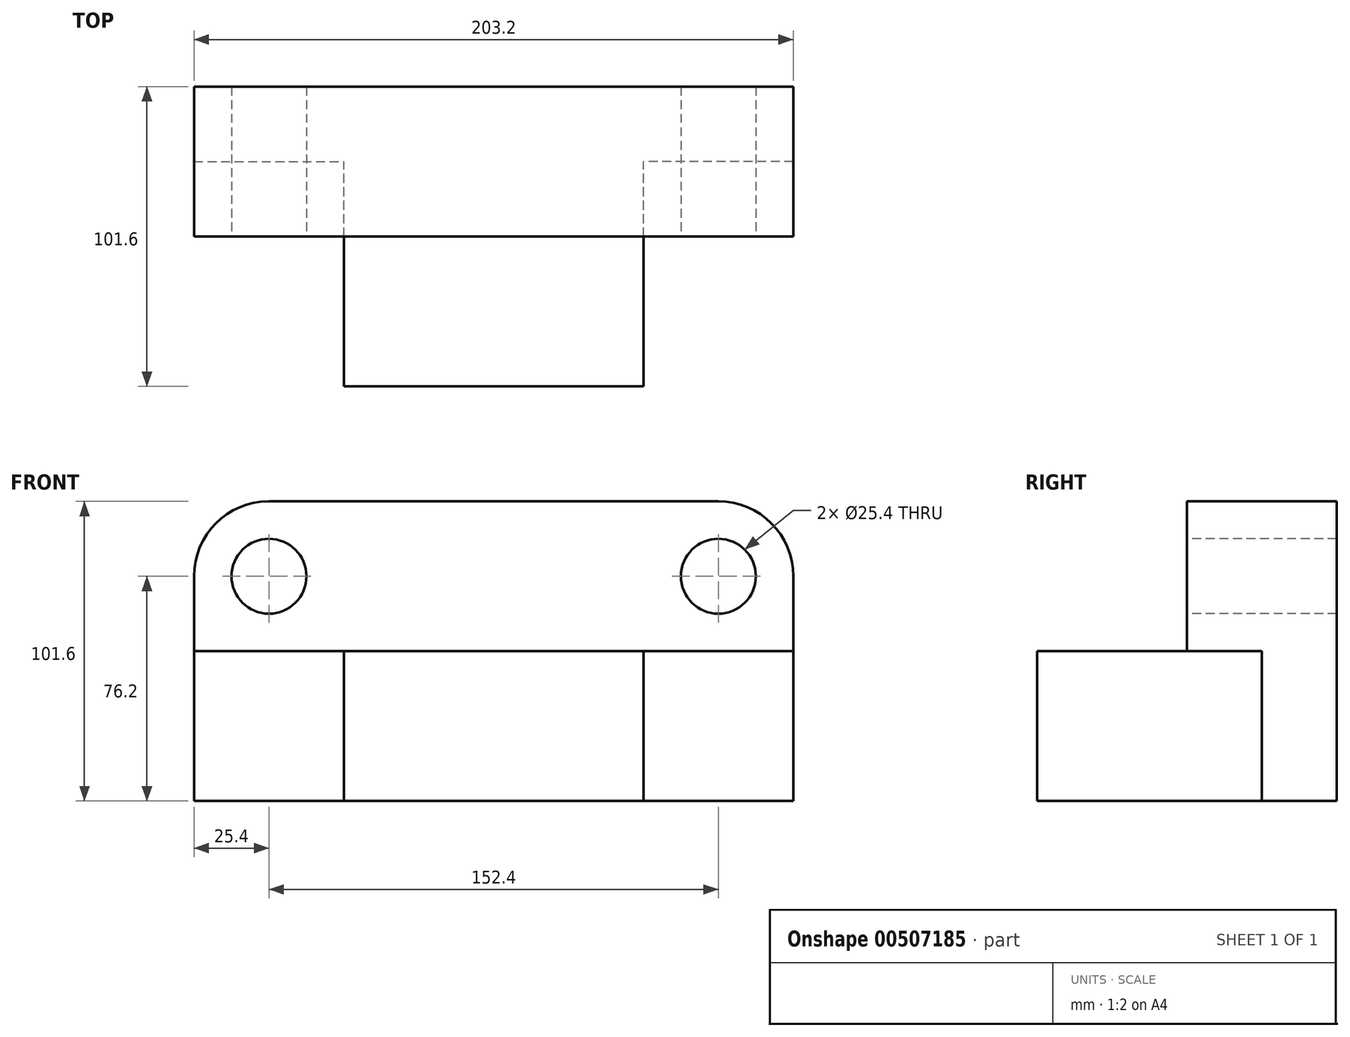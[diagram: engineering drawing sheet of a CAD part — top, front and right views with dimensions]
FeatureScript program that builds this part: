
annotation { "Feature Type Name" : "Feature", "Feature Type Description" : "" }
export const myFeature = defineFeature(function(context is Context, id is Id, definition is map)
    precondition{}
    {
        {
            var Q0;
            Q0=qCreatedBy(makeId("Top.planeOp"),FACE);
            var sketch = newSketch(context, id + "F0", { "sketchPlane" : qUnion([Q0])});
            skLineSegment(sketch, "E0.bottom", {"start": v(0, 0) * mm, "end": v(203.2, 0) * mm});
            skLineSegment(sketch, "E0.top", {"start": v(0, -101.6) * mm, "end": v(203.2, -101.6) * mm});
            skLineSegment(sketch, "E0.left", {"start": v(0, 0) * mm, "end": v(0, -101.6) * mm});
            skLineSegment(sketch, "E0.right", {"start": v(203.2, 0) * mm, "end": v(203.2, -101.6) * mm});
            skSolve(sketch);
        }
        {
            var Q0;
            Q0=makeQuery(id+"F0.imprint","IMPRINT",FACE,{"disambiguationData":[TD([[makeQuery(id+"F0.imprint","IMPRINT",EDGE,{"derivedFrom":sQuery(id+"F0.wireOp",EDGE,"E0.bottom")}),-1.0]])]});
            extrude(context, id + "F1", {"entities" : qUnion([Q0]), "depth" : 101.6 * mm});
        }
        {
            var Q0;
            Q0=makeQuery(id+"F1.opExtrude","CAP_FACE",FACE,{"disambiguationData":[OSD([sQuery(id+"F0.wireOp",EDGE,"E0.bottom"),sQuery(id+"F0.wireOp",EDGE,"E0.top"),sQuery(id+"F0.wireOp",EDGE,"E0.left"),sQuery(id+"F0.wireOp",EDGE,"E0.right")])],"isStart":true});
            var sketch = newSketch(context, id + "F2", { "sketchPlane" : qUnion([Q0])});
            skLineSegment(sketch, "E1.bottom", {"start": v(203.2, 101.6) * mm, "end": v(152.4, 101.6) * mm});
            skLineSegment(sketch, "E1.top", {"start": v(203.2, 25.4) * mm, "end": v(152.4, 25.4) * mm});
            skLineSegment(sketch, "E1.left", {"start": v(203.2, 101.6) * mm, "end": v(203.2, 25.4) * mm});
            skLineSegment(sketch, "E1.right", {"start": v(152.4, 101.6) * mm, "end": v(152.4, 25.4) * mm});
            skSolve(sketch);
        }
        {
            var Q0;
            Q0=makeQuery(id+"F2.imprint","IMPRINT",FACE,{"disambiguationData":[TD([[makeQuery(id+"F2.imprint","IMPRINT",EDGE,{"derivedFrom":sQuery(id+"F2.wireOp",EDGE,"E1.bottom")}),-1.0]])]});
            extrude(context, id + "F3", {"entities" : qUnion([Q0]), "operationType" : NewBodyOperationType.REMOVE, "oppositeDirection" : true, "depth" : 50.8 * mm});
        }
        {
            var Q0;
            Q0=makeQuery(id+"F1.opExtrude","CAP_FACE",FACE,{"disambiguationData":[OSD([sQuery(id+"F0.wireOp",EDGE,"E0.bottom"),sQuery(id+"F0.wireOp",EDGE,"E0.top"),sQuery(id+"F0.wireOp",EDGE,"E0.left"),sQuery(id+"F0.wireOp",EDGE,"E0.right")])],"isStart":true});
            var sketch = newSketch(context, id + "F4", { "sketchPlane" : qUnion([Q0])});
            skLineSegment(sketch, "E2.bottom", {"start": v(0, 101.6) * mm, "end": v(50.8, 101.6) * mm});
            skLineSegment(sketch, "E2.top", {"start": v(0, 25.4) * mm, "end": v(50.8, 25.4) * mm});
            skLineSegment(sketch, "E2.left", {"start": v(0, 101.6) * mm, "end": v(0, 25.4) * mm});
            skLineSegment(sketch, "E2.right", {"start": v(50.8, 101.6) * mm, "end": v(50.8, 25.4) * mm});
            skSolve(sketch);
        }
        {
            var Q0;
            Q0=makeQuery(id+"F4.imprint","IMPRINT",FACE,{"disambiguationData":[TD([[makeQuery(id+"F4.imprint","IMPRINT",EDGE,{"derivedFrom":sQuery(id+"F4.wireOp",EDGE,"E2.bottom")}),-1.0]])]});
            extrude(context, id + "F5", {"entities" : qUnion([Q0]), "operationType" : NewBodyOperationType.REMOVE, "oppositeDirection" : true, "depth" : 50.8 * mm});
        }
        {
            var Q0;
            Q0=makeQuery(id+"F1.opExtrude","CAP_EDGE",EDGE,{"disambiguationData":[OSD([sQuery(id+"F0.wireOp",EDGE,"E0.right")])],"isStart":false});
            fillet(context, id + "F6", {"entities" : qUnion([Q0]), "radius" : 25.4 * mm, "tangentPropagation" : true, "allowEdgeOverflow" : false});
        }
        {
            var Q0;
            Q0=makeQuery(id+"F1.opExtrude","CAP_EDGE",EDGE,{"disambiguationData":[OSD([sQuery(id+"F0.wireOp",EDGE,"E0.left")])],"isStart":false});
            fillet(context, id + "F7", {"entities" : qUnion([Q0]), "radius" : 25.4 * mm, "tangentPropagation" : true, "allowEdgeOverflow" : false});
        }
        {
            var Q0;
            Q0=makeQuery(id+"F4PwHQEw8X9MmWq_1.boolean.opBoolean","COPY",FACE,{"derivedFrom":makeQuery(id+"F4PwHQEw8X9MmWq_1.opExtrude","SWEPT_FACE",FACE,{"disambiguationData":[OSD([sQuery(id+"FQOh0idirYJ9PJE_1.wireOp",EDGE,"Frty84uf-Vyrj-mid0-v118-2i0YeY8wPQO7.top")])]})});
            var sketch = newSketch(context, id + "F8", { "sketchPlane" : qUnion([Q0])});
            skCircle(sketch, "E3", {"center": v(25.4, 76.2) * mm, "radius": 12.7 * mm});
            skSolve(sketch);
        }
        {
            var Q0;
            Q0=makeQuery(id+"F1.opExtrude","SWEPT_FACE",FACE,{"disambiguationData":[OSD([sQuery(id+"F0.wireOp",EDGE,"E0.top")])]});
            var sketch = newSketch(context, id + "F9", { "sketchPlane" : qUnion([Q0])});
            skLineSegment(sketch, "E4", {"start": v(50.8, 50.8) * mm, "end": v(152.4, 50.8) * mm});
            skSolve(sketch);
        }
        {
            var Q0;
            Q0=makeQuery(id+"F9.imprint","IMPRINT",FACE,{"disambiguationData":[TD([[makeQuery(id+"F9.imprint","IMPRINT",EDGE,{"derivedFrom":sQuery(id+"F9.wireOp",EDGE,"E4")}),1.0]])]});
            extrude(context, id + "F10", {"entities" : qUnion([Q0]), "operationType" : NewBodyOperationType.REMOVE, "oppositeDirection" : true, "depth" : 50.8 * mm, "offsetDistance" : 25.4 * mm});
        }
        {
            var Q0;
            Q0=makeQuery(id+"F10.boolean.opBoolean","COPY",FACE,{"derivedFrom":makeQuery(id+"F10.opExtrude","CAP_FACE",FACE,{"disambiguationData":[OSD([sQuery(id+"F0.wireOp",EDGE,"E0.top"),sQuery(id+"F0.wireOp",EDGE,"E0.left"),sQuery(id+"F0.wireOp",EDGE,"E0.right"),sQuery(id+"F2.wireOp",EDGE,"E1.bottom"),sQuery(id+"F4.wireOp",EDGE,"E2.bottom"),sQuery(id+"F9.wireOp",EDGE,"E4")])],"isStart":false})});
            var sketch = newSketch(context, id + "F11", { "sketchPlane" : qUnion([Q0])});
            skCircle(sketch, "E5", {"center": v(25.4, 76.2) * mm, "radius": 12.7 * mm});
            skSolve(sketch);
        }
        {
            var Q0;
            Q0=makeQuery(id+"F11.imprint","IMPRINT",FACE,{"disambiguationData":[TD([[makeQuery(id+"F11.imprint","IMPRINT",EDGE,{"derivedFrom":sQuery(id+"F11.wireOp",EDGE,"E5")}),1.0]])]});
            extrude(context, id + "F12", {"entities" : qUnion([Q0]), "operationType" : NewBodyOperationType.REMOVE, "oppositeDirection" : true, "depth" : 50.8 * mm, "offsetDistance" : 25.4 * mm});
        }
        {
            var Q0;
            Q0=makeQuery(id+"F10.boolean.opBoolean","COPY",FACE,{"derivedFrom":makeQuery(id+"F10.opExtrude","CAP_FACE",FACE,{"disambiguationData":[OSD([sQuery(id+"F0.wireOp",EDGE,"E0.top"),sQuery(id+"F0.wireOp",EDGE,"E0.left"),sQuery(id+"F0.wireOp",EDGE,"E0.right"),sQuery(id+"F2.wireOp",EDGE,"E1.bottom"),sQuery(id+"F4.wireOp",EDGE,"E2.bottom"),sQuery(id+"F9.wireOp",EDGE,"E4")])],"isStart":false})});
            var sketch = newSketch(context, id + "F13", { "sketchPlane" : qUnion([Q0])});
            skCircle(sketch, "E6", {"center": v(177.8, 76.2) * mm, "radius": 12.7 * mm});
            skSolve(sketch);
        }
        {
            var Q0;
            Q0=makeQuery(id+"F13.imprint","IMPRINT",FACE,{"disambiguationData":[TD([[makeQuery(id+"F13.imprint","IMPRINT",EDGE,{"derivedFrom":sQuery(id+"F13.wireOp",EDGE,"E6")}),1.0]])]});
            extrude(context, id + "F14", {"entities" : qUnion([Q0]), "operationType" : NewBodyOperationType.REMOVE, "oppositeDirection" : true, "depth" : 50.8 * mm, "offsetDistance" : 25.4 * mm});
        }
    });
